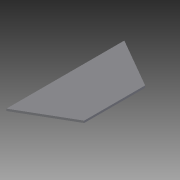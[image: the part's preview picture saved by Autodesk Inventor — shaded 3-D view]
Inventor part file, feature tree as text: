
AUTODESK INVENTOR PART (.ipt)
format: ipt  version: 2016 (Build 200138000, 138)  size: 71,168 bytes
history: native  units: in
note: dims shown in document units (in); Inventor stores cm internally (conversion verified against a paired STEP export)
features: extrude x1, sketch x1
ambient origin geometry x8: Origin, YZ Plane, XZ Plane, XY Plane, X Axis, Y Axis, Z Axis, Center Point
bodies: Solid1 (feature_tree)
feature tree (2):
  extrude  "Extrusion1"  TaperAngle=30.0deg  [1 undecoded]
  sketch  "Sketch1"  dims[d0=120.0deg d1=30.0deg d3=7.0in d4=0.25in d5=0.0in d6=5.0in]
note: 1 required parameter value undecoded (feature->parameter linkage not recoverable at this tier; creation-order binding heuristic only, values carry confidence <= 0.55)
